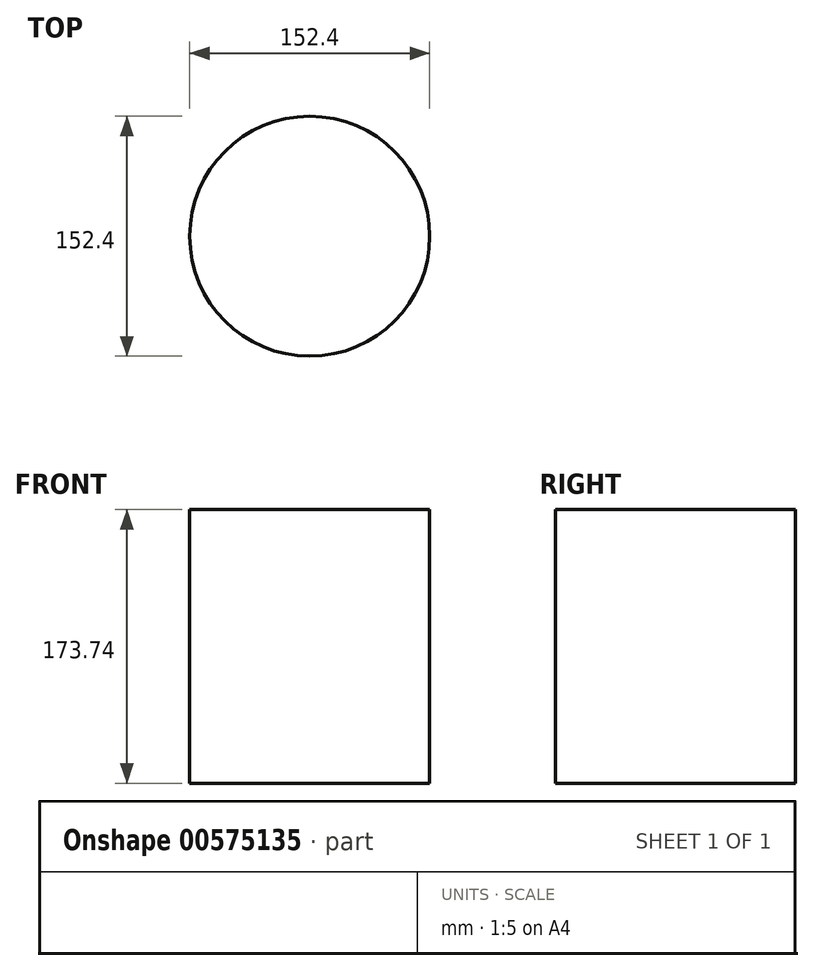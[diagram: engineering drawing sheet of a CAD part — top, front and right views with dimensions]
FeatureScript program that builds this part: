
annotation { "Feature Type Name" : "Feature", "Feature Type Description" : "" }
export const myFeature = defineFeature(function(context is Context, id is Id, definition is map)
    precondition{}
    {
        {
            var Q0;
            Q0=qCreatedBy(makeId("Top.planeOp"),FACE);
            var sketch = newSketch(context, id + "F0", { "sketchPlane" : qUnion([Q0])});
            skCircle(sketch, "E0", {"center": v(0, 0) * mm, "radius": 76.2 * mm});
            skSolve(sketch);
        }
        {
            var Q0;
            Q0=makeQuery(id+"F0.imprint","IMPRINT",FACE,{"disambiguationData":[TD([[makeQuery(id+"F0.imprint","IMPRINT",EDGE,{"derivedFrom":sQuery(id+"F0.wireOp",EDGE,"E0")}),1.0]])]});
            extrude(context, id + "F1", {"entities" : qUnion([Q0]), "endBound" : BoundingType.SYMMETRIC, "depth" : 173.74 * mm, "offsetDistance" : 30.48 * mm});
        }
    });
